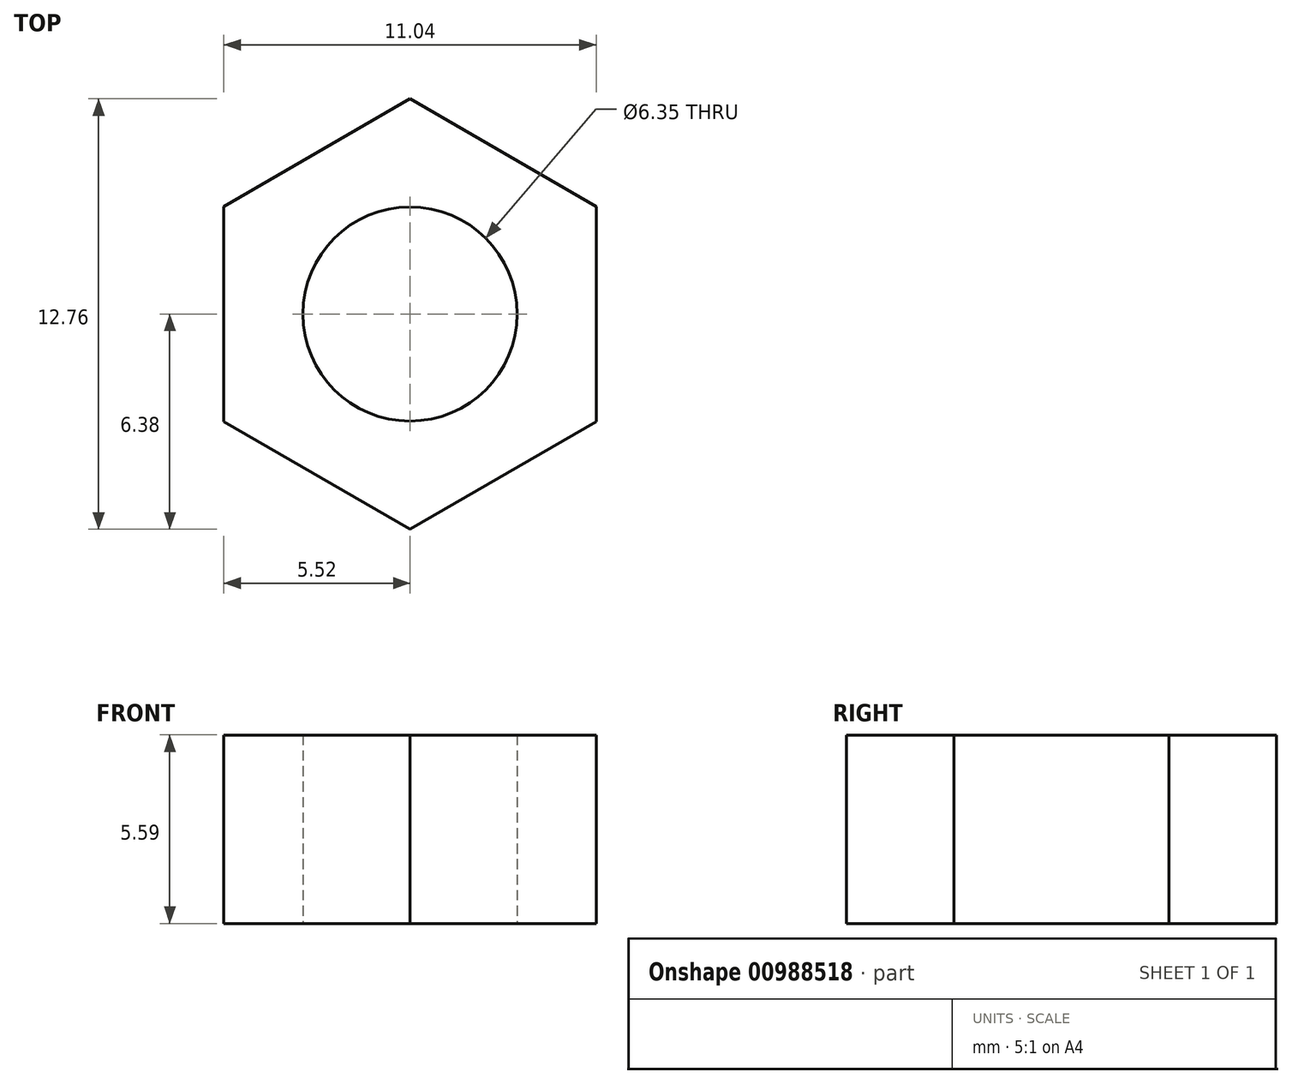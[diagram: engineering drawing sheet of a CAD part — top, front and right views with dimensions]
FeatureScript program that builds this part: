
annotation { "Feature Type Name" : "Feature", "Feature Type Description" : "" }
export const myFeature = defineFeature(function(context is Context, id is Id, definition is map)
    precondition{}
    {
        {
            var Q0;
            Q0=qCreatedBy(makeId("Top.planeOp"),FACE);
            var sketch = newSketch(context, id + "F0", { "sketchPlane" : qUnion([Q0])});
            skCircle(sketch, "E0.cCircle", {"center": v(0, 0) * mm, "radius": 5.52 * mm, "construction": true});
            skLineSegment(sketch, "E0.0", {"start": v(5.52, -3.19) * mm, "end": v(0, -6.38) * mm});
            skLineSegment(sketch, "E0.1", {"start": v(0, -6.38) * mm, "end": v(-5.52, -3.19) * mm});
            skLineSegment(sketch, "E0.2", {"start": v(-5.52, -3.19) * mm, "end": v(-5.52, 3.19) * mm});
            skLineSegment(sketch, "E0.3", {"start": v(-5.52, 3.19) * mm, "end": v(0, 6.38) * mm});
            skLineSegment(sketch, "E0.4", {"start": v(0, 6.38) * mm, "end": v(5.52, 3.19) * mm});
            skLineSegment(sketch, "E0.5", {"start": v(5.52, 3.19) * mm, "end": v(5.52, -3.19) * mm});
            skPoint(sketch, "E0.0.midPoint", {"position": v(2.76, -4.78) * mm});
            skCircle(sketch, "E1", {"center": v(0, 0) * mm, "radius": 3.18 * mm});
            skSolve(sketch);
        }
        {
            var Q0;
            Q0=qSketchRegion(id+"F0",true);
            extrude(context, id + "F1", {"entities" : qUnion([Q0]), "depth" : 5.6 * mm, "offsetDistance" : 25.4 * mm});
        }
    });
